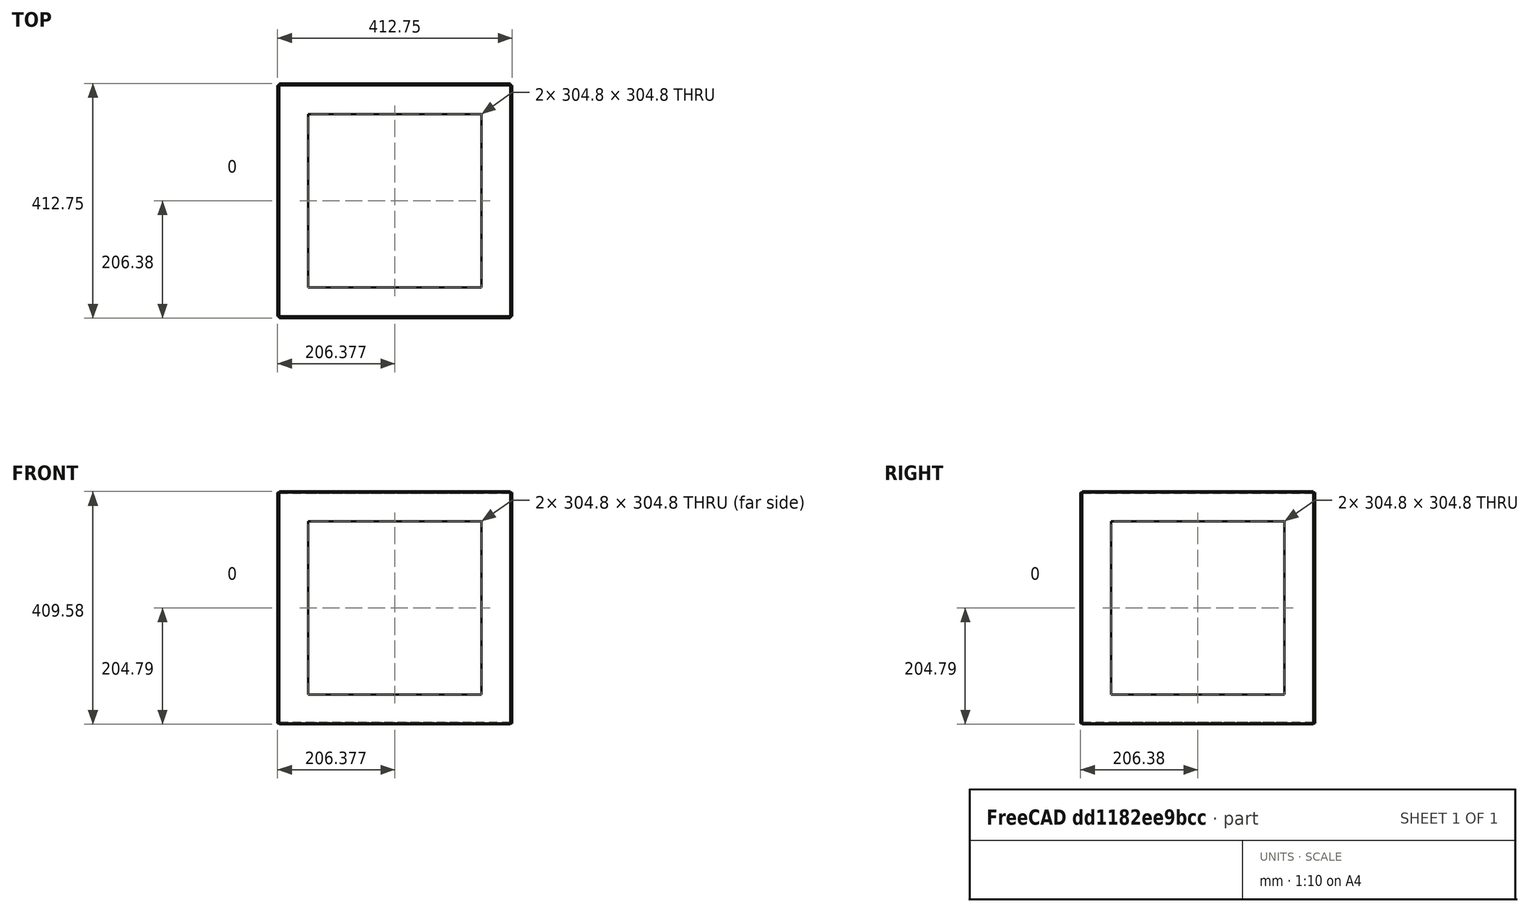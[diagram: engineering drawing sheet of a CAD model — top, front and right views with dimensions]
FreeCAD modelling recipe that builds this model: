
FCSTD DOCUMENT  (FreeCAD 0.16R6707 (Git))
Label: D3D Complete Frame 16in
License: CreativeCommons Attribution
LicenseURL: http://creativecommons.org/licenses/by/4.0/
objects: Part::FeaturePython×5, Sketcher::SketchObject×1, PartDesign::Pad×1, Part::MultiFuse×1
note: 9 computed .brp shape members not serialized (recipe doc carries the construction recipe); baked Part::Feature solids carry a one-line shape summary decoded from their .brp

FEATURE [Sketcher::SketchObject] Sketch
  Placement = pos=(0,0,0) rot=(0.57735,0.57735,0.57735;2.0944rad)
  sketch-geometry (8):
    g0: LineSegment StartX=0 StartY=406.4 StartZ=0 EndX=406.4 EndY=406.4 EndZ=0
    g1: LineSegment StartX=406.4 StartY=406.4 StartZ=0 EndX=406.4 EndY=0 EndZ=0
    g2: LineSegment StartX=406.4 StartY=0 StartZ=0 EndX=0 EndY=0 EndZ=0
    g3: LineSegment StartX=0 StartY=0 StartZ=0 EndX=0 EndY=406.4 EndZ=0
    g4: LineSegment StartX=50.8 StartY=355.6 StartZ=0 EndX=355.6 EndY=355.6 EndZ=0
    g5: LineSegment StartX=355.6 StartY=355.6 StartZ=0 EndX=355.6 EndY=50.8 EndZ=0
    g6: LineSegment StartX=355.6 StartY=50.8 StartZ=0 EndX=50.8 EndY=50.8 EndZ=0
    g7: LineSegment StartX=50.8 StartY=50.8 StartZ=0 EndX=50.8 EndY=355.6 EndZ=0
  constraints (23):
    c: Coincident(g0,g1)
    c: Coincident(g1,g2)
    c: Coincident(g2,g3)
    c: Coincident(g3,g0)
    c: Horizontal(g0)
    c: Horizontal(g2)
    c: Vertical(g1)
    c: Vertical(g3)
    c: Equal(g0,g3)
    c: DistanceX(g0,g0) = 406.4
    c: Coincident(g4,g5)
    c: Coincident(g5,g6)
    c: Coincident(g6,g7)
    c: Coincident(g7,g4)
    c: Horizontal(g4)
    c: Horizontal(g6)
    c: Vertical(g5)
    c: Vertical(g7)
    c: DistanceX(g0,g4) = 50.8
    c: Equal(g4,g7)
    c: Coincident(g2,g-1)
    c: DistanceY(g4,g0) = 50.8
    c: DistanceX(g4,g4) = 304.8
FEATURE [PartDesign::Pad] Pad  label="Left Frame"
  Length = 3.175
  Length2 = 100
  Midplane = true
  Placement = pos=(0,0,0) rot=(0.57735,0.57735,0.57735;2.0944rad)
  Sketch = -> Sketch
  Type = 0
FEATURE [Part::FeaturePython] Clone  label="Right Frame"  # Draft clone (typed FeaturePython)
  Objects = -> [Pad]
  Placement = pos=(409.575,0,0) rot=(0.57735,0.57735,0.57735;2.0944rad)
  Scale = (1,1,1)
FEATURE [Part::FeaturePython] Clone001  label="Front Frame"  # Draft clone (typed FeaturePython)
  Objects = -> [Pad]
  Placement = pos=(1.5875,-1.5875,0) rot=(1,0,0;1.5708rad)
  Scale = (1,1,1)
FEATURE [Part::FeaturePython] Clone002  label="Back Frame"  # Draft clone (typed FeaturePython)
  Objects = -> [Pad]
  Placement = pos=(1.5875,407.987,0) rot=(-0.57735,-0.57735,-0.57735;2.0944rad)
  Scale = (1,1,1)
FEATURE [Part::FeaturePython] Clone003  label="Bottom frame"  # Draft clone (typed FeaturePython)
  Objects = -> [Pad]
  Placement = pos=(1.5875,0,0) rot=(0,0,1;0rad)
  Scale = (1,1,1)
FEATURE [Part::FeaturePython] Clone004  label="Top Frame"  # Draft clone (typed FeaturePython)
  Objects = -> [Clone003]
  Placement = pos=(1.5875,0,406.4) rot=(0,0,1;0rad)
  Scale = (1,1,1)
FEATURE [Part::MultiFuse] Fusion005  label="Frame"
  Shapes = -> [Clone003,Clone002,Clone001,Clone,Pad,Clone004]
